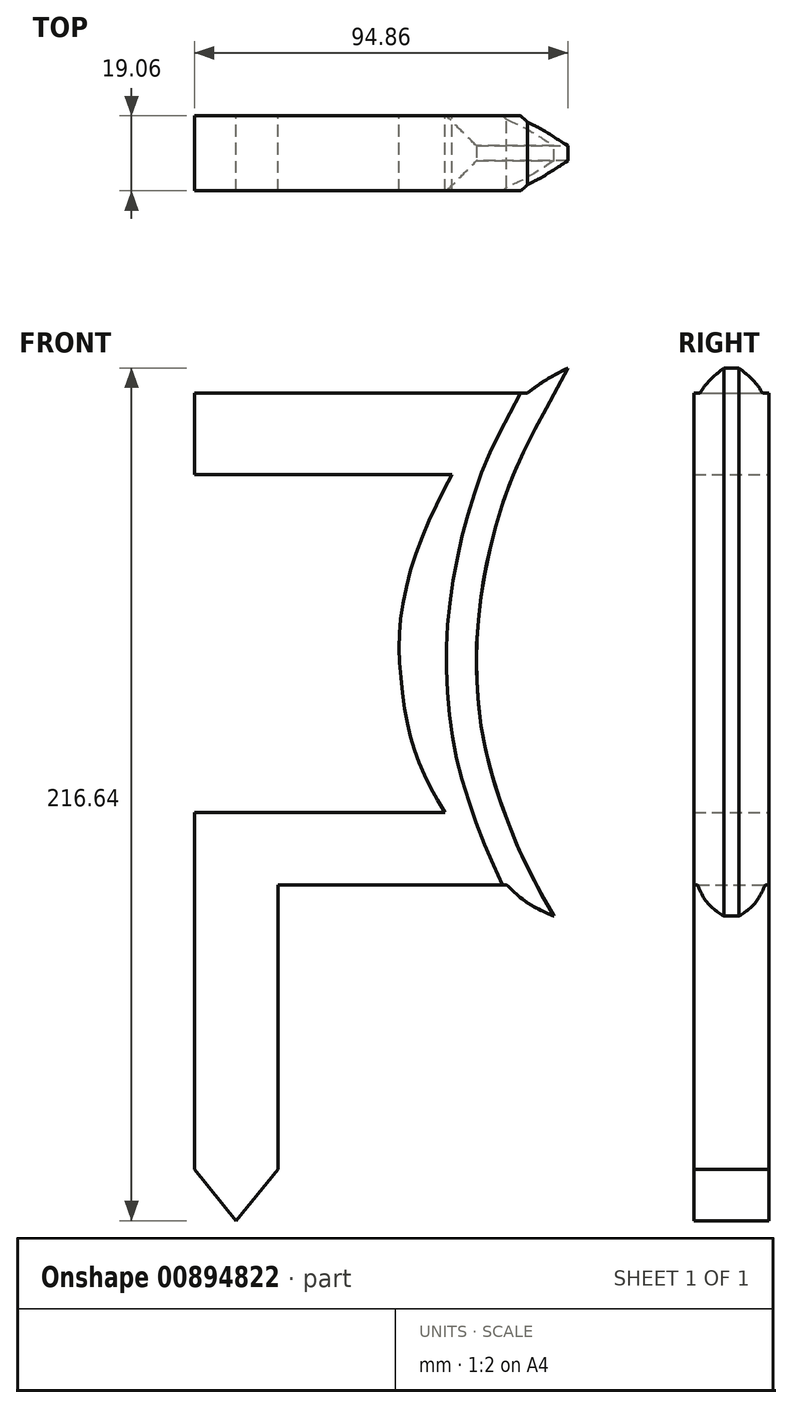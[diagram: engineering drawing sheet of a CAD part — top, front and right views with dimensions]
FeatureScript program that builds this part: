
annotation { "Feature Type Name" : "Feature", "Feature Type Description" : "" }
export const myFeature = defineFeature(function(context is Context, id is Id, definition is map)
    precondition{}
    {
        {
            var Q0;
            Q0=qCreatedBy(makeId("Front.planeOp"),FACE);
            var sketch = newSketch(context, id + "F0", { "sketchPlane" : qUnion([Q0])});
            skLineSegment(sketch, "E0", {"start": v(-12.93, 10.97) * mm, "end": v(10.47, 10.97) * mm});
            skLineSegment(sketch, "E1", {"start": v(10.47, 10.97) * mm, "end": v(71.69, 10.97) * mm});
            skFitSpline(sketch, "E2", {"points": [v(71.69, 10.97) * mm, v(75.78, 13.93) * mm, v(81.93, 17.32) * mm], "startDerivative": vector(8.34, 6.51) * mm, "endDerivative": vector(12.04, 6.2) * mm});
            skFitSpline(sketch, "E3", {"points": [v(81.93, 17.32) * mm, v(75.65, 5.53) * mm, v(68.2, -9.39) * mm, v(62.77, -26) * mm, v(59.88, -40.59) * mm, v(58.7, -55.68) * mm, v(60.1, -75.05) * mm, v(64.21, -91.12) * mm, v(70.6, -107.34) * mm, v(78.37, -121.96) * mm], "startDerivative": vector(-60.52, -114.31) * mm, "endDerivative": vector(72.3, -127.63) * mm});
            skFitSpline(sketch, "E4", {"points": [v(78.37, -121.96) * mm, v(71.69, -118.58) * mm, v(66.35, -113.98) * mm], "startDerivative": vector(-13.76, 5.98) * mm, "endDerivative": vector(-10.28, 9.98) * mm});
            skLineSegment(sketch, "E5", {"start": v(66.35, -113.98) * mm, "end": v(-2.33, -113.98) * mm});
            skLineSegment(sketch, "E6", {"start": v(-12.93, 10.97) * mm, "end": v(-12.93, -113.98) * mm});
            skLineSegment(sketch, "E7", {"start": v(-12.93, -113.98) * mm, "end": v(-2.33, -113.98) * mm});
            skFitSpline(sketch, "E8", {"points": [v(52.5, -9.73) * mm, v(44.42, -26.85) * mm, v(39.6, -44.93) * mm, v(39.24, -58.43) * mm, v(41.21, -73.26) * mm, v(44.64, -84.35) * mm, v(50.72, -95.57) * mm], "startDerivative": vector(-46.13, -88.67) * mm, "endDerivative": vector(43.2, -73.22) * mm});
            skLineSegment(sketch, "E9", {"start": v(52.5, -9.73) * mm, "end": v(10.47, -9.73) * mm});
            skLineSegment(sketch, "E10", {"start": v(50.72, -95.57) * mm, "end": v(10.47, -95.57) * mm});
            skLineSegment(sketch, "E11", {"start": v(10.47, -95.57) * mm, "end": v(10.47, -9.73) * mm});
            skLineSegment(sketch, "E12", {"start": v(-12.93, -113.98) * mm, "end": v(-12.93, -186.32) * mm});
            skLineSegment(sketch, "E13", {"start": v(-12.93, -186.32) * mm, "end": v(-1.82, -199.95) * mm});
            skLineSegment(sketch, "E14", {"start": v(-2.33, -113.98) * mm, "end": v(-2.33, -106.8) * mm});
            skLineSegment(sketch, "E15.MirrorCS", {"start": v(8.28, -113.98) * mm, "end": v(8.28, -186.32) * mm});
            skLineSegment(sketch, "E16.MirrorCS", {"start": v(8.28, -186.32) * mm, "end": v(-2.84, -199.95) * mm});
            skLineSegment(sketch, "E17", {"start": v(10.47, -9.73) * mm, "end": v(-12.93, -9.73) * mm});
            skLineSegment(sketch, "E18", {"start": v(10.47, -95.57) * mm, "end": v(-12.93, -95.57) * mm});
            skSolve(sketch);
        }
        {
            var Q0;
            Q0=makeQuery(id+"F0.imprint","IMPRINT",FACE,{"disambiguationData":[TD([[makeQuery(id+"F0.imprint","IMPRINT",EDGE,{"derivedFrom":sQuery(id+"F0.wireOp",EDGE,"E0")}),-1.0]])]});
            var Q1;
            {var subQ4=sQuery(id+"F0.wireOp",EDGE,"E7");Q1=makeQuery(id+"F0.imprint","IMPRINT",FACE,{"disambiguationData":[TD([[makeQuery(id+"F0.imprint","IMPRINT",EDGE,{"derivedFrom":subQ4}),-1.0]])]});}
            extrude(context, id + "F1", {"entities" : qUnion([Q0, Q1]), "endBound" : BoundingType.SYMMETRIC, "depth" : 19.05 * mm, "offsetDistance" : 25.4 * mm});
        }
        {
            var Q0;
            Q0=makeQuery(id+"F1.opExtrude","CAP_EDGE",EDGE,{"disambiguationData":[OSD([sQuery(id+"F0.wireOp",EDGE,"E3")])],"isStart":false});
            var Q1;
            Q1=makeQuery(id+"F1.opExtrude","CAP_EDGE",EDGE,{"disambiguationData":[OSD([sQuery(id+"F0.wireOp",EDGE,"E3")])],"isStart":true});
            chamfer(context, id + "F2", {"entities" : qUnion([Q0, Q1]), "width" : 7.62 * mm, "tangentPropagation" : true});
        }
    });
